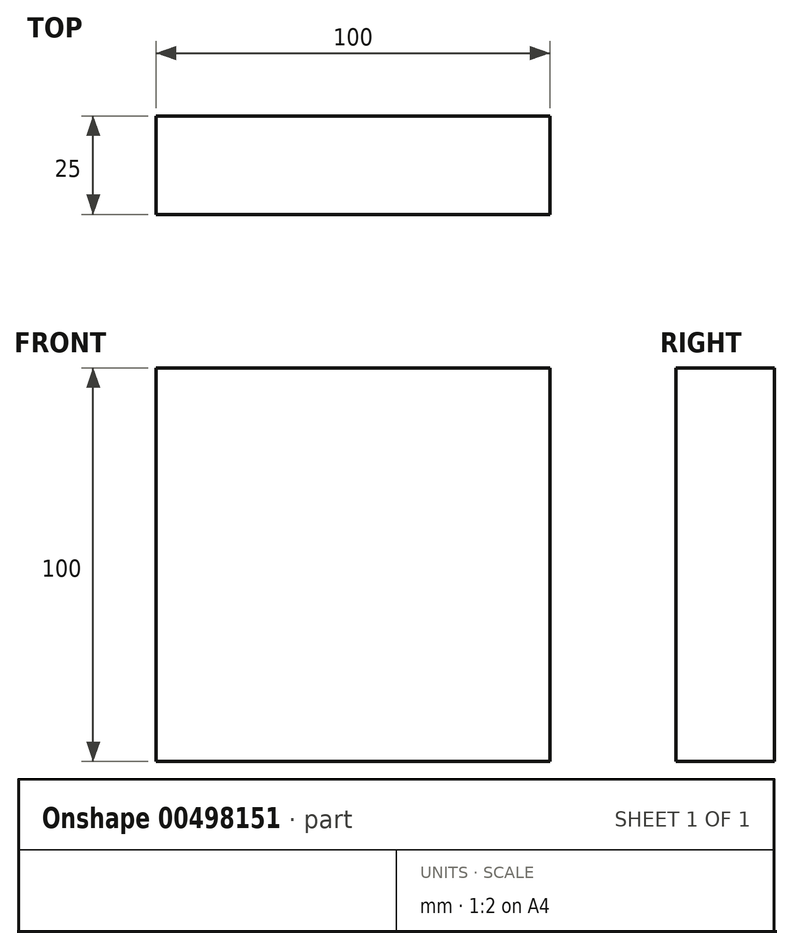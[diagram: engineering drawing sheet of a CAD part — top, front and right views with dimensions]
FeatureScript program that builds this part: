
annotation { "Feature Type Name" : "Feature", "Feature Type Description" : "" }
export const myFeature = defineFeature(function(context is Context, id is Id, definition is map)
    precondition{}
    {
        {
            var Q0;
            Q0=qCreatedBy(makeId("Front.planeOp"),FACE);
            var sketch = newSketch(context, id + "F0", { "sketchPlane" : qUnion([Q0])});
            skLineSegment(sketch, "E0.bottom", {"start": v(-50, 50) * mm, "end": v(50, 50) * mm});
            skLineSegment(sketch, "E0.top", {"start": v(-50, -50) * mm, "end": v(50, -50) * mm});
            skLineSegment(sketch, "E0.left", {"start": v(-50, 50) * mm, "end": v(-50, -50) * mm});
            skLineSegment(sketch, "E0.right", {"start": v(50, 50) * mm, "end": v(50, -50) * mm});
            skLineSegment(sketch, "E1", {"start": v(-50, 50) * mm, "end": v(50, -50) * mm, "construction": true});
            skSolve(sketch);
        }
        {
            var Q0;
            Q0 = qSketchRegion(id + "F0", true);
            extrude(context, id + "F1", {"entities" : qUnion([Q0]), "depth" : 25 * mm});
        }
    });
